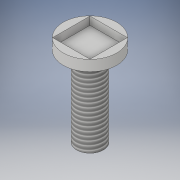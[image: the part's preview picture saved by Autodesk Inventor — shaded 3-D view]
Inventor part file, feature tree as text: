
AUTODESK INVENTOR PART (.ipt)
format: ipt  version: 2019 (Build 230136000, 136)  size: 117,248 bytes
history: native  units: in
note: dims shown in document units (in); Inventor stores cm internally (conversion verified against a paired STEP export)
features: extrude x3, sketch x3, thread x1
ambient origin geometry x8: Origin, YZ Plane, XZ Plane, XY Plane, X Axis, Y Axis, Z Axis, Center Point
bodies: Solid1 (feature_tree)
feature tree (7):
  extrude  "Extrusion1"  Depth=0.2in TaperAngle=0.0deg
  extrude  "Extrusion2"  Depth=0.5in
  extrude  "Extrusion3"  Depth=1.5in TaperAngle=0.0deg
  thread  "Thread1"  [1 undecoded]
  sketch  "Sketch1"  dims[d0=1.0in d1=0.2in d2=0.0in]
  sketch  "Sketch2"  dims[d7=0.15in d8=0.0in d9=0.5in]
  sketch  "Sketch3"  dims[d10=1.5in d11=0.0in d12=1.0in d13=0.0in]
note: 1 required parameter value undecoded (feature->parameter linkage not recoverable at this tier; creation-order binding heuristic only, values carry confidence <= 0.55)
